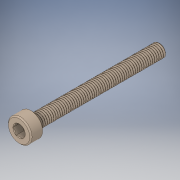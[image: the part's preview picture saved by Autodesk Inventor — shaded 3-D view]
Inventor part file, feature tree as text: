
AUTODESK INVENTOR PART (.ipt)
format: ipt  version: 2019 (Build 230136000, 136)  size: 663,552 bytes
history: mixed  units: mm
features: chamfer x1, imported_body x1
ambient origin geometry x8: Origin, YZ Plane, XZ Plane, XY Plane, X Axis, Y Axis, Z Axis, Center Point
bodies: Solid1 (imported_parasolid)
feature tree (2):
  chamfer  "Chamfer1"  [1 undecoded]
  imported_body  NMx_Import_Brep_tag  [imported B-rep: ~3 faces, bbox_mm=None]
note: 1 required parameter value undecoded (feature->parameter linkage not recoverable at this tier; creation-order binding heuristic only, values carry confidence <= 0.55)
